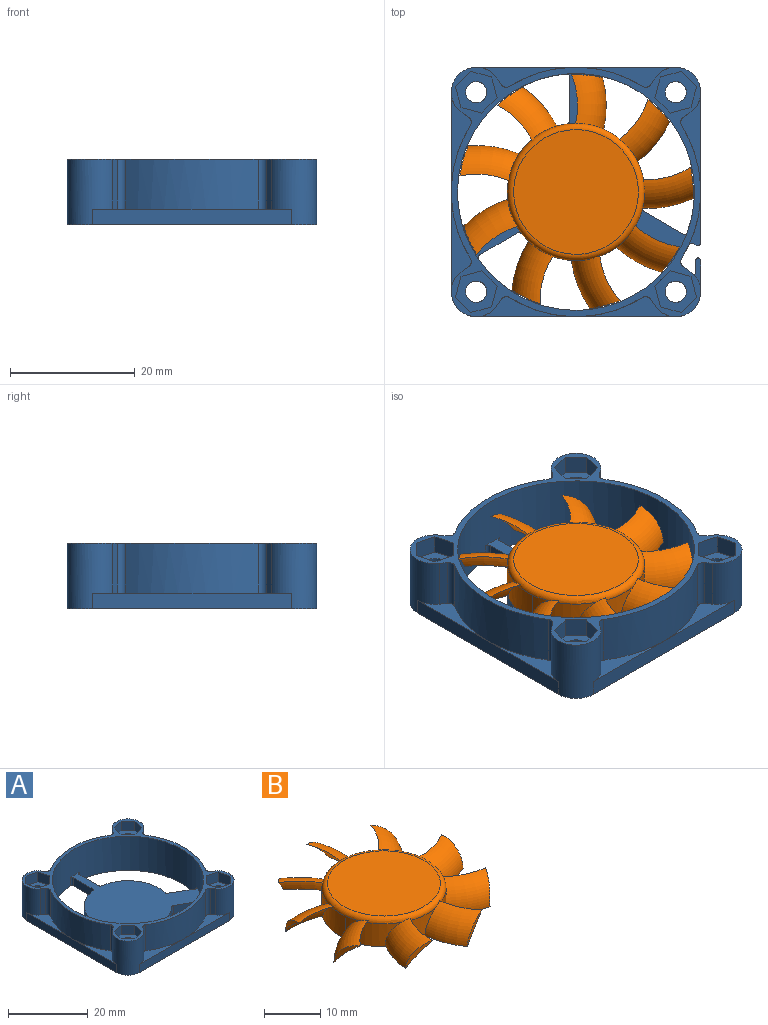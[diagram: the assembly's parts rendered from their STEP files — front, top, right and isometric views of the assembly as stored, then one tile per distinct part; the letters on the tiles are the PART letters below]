
ASSEMBLY  parts=2 mates=1
PART A: 115 faces, bbox 40x40x10.5 mm
  f0: plane 10.28x5.94mm, normal (0.5,0.87,0), area 17.8mm2, adj f19,f33,f35,f80,f81,f82
  f1: plane 2.5x1.78mm, normal (-1,0,0), area 4.5mm2, adj f8,f33,f81,f97
  f2: plane 16x3.21mm, normal (0,0,1), area 18mm2, adj f26,f27,f56,f57,f100
  f3: plane 16x3.21mm, normal (0,0,1), area 18mm2, adj f25,f26,f65,f69,f106
  f4: plane 16x3.21mm, normal (0,0,1), area 18mm2, adj f21,f22,f34,f60,f102
  f5: plane 16x3.21mm, normal (0,0,1), area 18mm2, adj f23,f24,f62,f63,f104
  f6: plane 16x3.21mm, normal (0,0,1), area 18mm2, adj f27,f28,f57,f58,f101
  f7: plane 35.04x31.24mm, normal (0,0,1), area 457.1mm2, adj f12,f13,f14,f15,f16,f17,f18,f30
  f8: plane 5.45x1.07mm, normal (0,0,1), area 3mm2, adj f1,f28,f29,f81,f96,f97
  f9: plane 16x3.21mm, normal (0,0,1), area 18mm2, adj f22,f23,f61,f62,f103
  f10: plane 8.58x1.89mm, normal (0,0,1), area 5.1mm2, adj f20,f21,f34,f76,f89
  f11: plane 16x3.21mm, normal (0,0,1), area 18mm2, adj f24,f25,f64,f65,f105
  f12: plane 7.04x2.5mm, normal (1,0,0), area 17.6mm2, adj f7,f33,f87,f92
  f13: cylinder r=19mm len=38mm, axis (0,0,1), area 1221.3mm2, adj f7,f33,f71,f83,f84,f85,f86,f87
  f14: plane 6.22x3.59mm, normal (0.5,0.87,0), area 18mm2, adj f7,f33,f88,f95
  f15: plane 6.09x3.52mm, normal (0.5,-0.87,0), area 17.6mm2, adj f7,f33,f84,f90
  f16: cylinder r=11mm len=16.31mm, axis (0,0,1), area 46.1mm2, adj f7,f33,f90,f94
  f17: plane 6.09x3.52mm, normal (-0.5,0.87,0), area 17.6mm2, adj f7,f33,f85,f91
  f18: plane 7.04x2.5mm, normal (-1,0,0), area 17.6mm2, adj f7,f33,f86,f93
  f19: cylinder r=11mm len=3.9mm, axis (0,0,1), area 6.7mm2, adj f0,f20,f33,f35,f77
  f20: plane 8.8x5.08mm, normal (-0.5,-0.87,0), area 11.1mm2, adj f10,f19,f33,f76,f77,f78,f89
  f21: plane 24.08x2.5mm, normal (1,0,0), area 60.2mm2, adj f4,f10,f22,f33,f89
  f22: cylinder r=4mm len=10.5mm, axis (0,0,1), area 127.6mm2, adj f4,f9,f21,f23,f33,f60,f61,f71
  f23: plane 32x2.5mm, normal (0,1,0), area 80mm2, adj f5,f9,f22,f24,f33
  f24: cylinder r=4mm len=10.5mm, axis (0,0,1), area 127.6mm2, adj f5,f11,f23,f25,f33,f63,f64,f71
  f25: plane 32x2.5mm, normal (-1,0,0), area 80mm2, adj f3,f11,f24,f26,f33
  f26: cylinder r=4mm len=10.5mm, axis (0,0,1), area 127.6mm2, adj f2,f3,f25,f27,f33,f56,f69,f71
  f27: plane 32x2.5mm, normal (0,-1,0), area 80mm2, adj f2,f6,f26,f28,f33
  f28: cylinder r=4mm len=10.5mm, axis (0,0,1), area 128mm2, adj f6,f8,f27,f29,f33,f58,f59,f71
  f29: plane 4.96x2.5mm, normal (1,0,0), area 12.4mm2, adj f8,f28,f33,f96
  f30: plane 6.22x3.59mm, normal (-0.5,-0.87,0), area 18mm2, adj f7,f33,f83,f94
  f31: cylinder r=11mm len=15.12mm, axis (0,0,1), area 50.4mm2, adj f7,f33,f91,f93
  f32: cylinder r=11mm len=13.49mm, axis (0,0,1), area 46.1mm2, adj f7,f33,f92,f95
  f33: plane 40x40mm, normal (0,0,-1), area 793.4mm2, adj f0,f1,f12,f13,f14,f15,f16,f17
  f34: cylinder r=20mm len=21.25mm, axis (0,0,1), area 180.4mm2, adj f4,f10,f71,f76,f79,f98,f102
  f35: plane 9.49x8.4mm, normal (0,0,-1), area 34.2mm2, adj f0,f19,f77,f79,f80
  f36: plane 3.35x3mm, normal (-0.26,-0.97,0), area 10.4mm2, adj f37,f70,f71,f75
  f37: plane 3.35x3mm, normal (-0.97,-0.26,0), area 10.4mm2, adj f36,f38,f71,f75
  f38: plane 3x2.45mm, normal (-0.71,0.71,0), area 10.4mm2, adj f37,f39,f71,f75
  f39: plane 3.35x3mm, normal (0.26,0.97,0), area 10.4mm2, adj f38,f40,f71,f75
  f40: plane 3.35x3mm, normal (0.97,0.26,0), area 10.4mm2, adj f39,f70,f71,f75
  f41: plane 3x2.45mm, normal (-0.71,0.71,0), area 10.4mm2, adj f42,f66,f71,f73
  f42: plane 3.35x3mm, normal (0.26,0.97,0), area 10.4mm2, adj f41,f43,f71,f73
  f43: plane 3.35x3mm, normal (0.97,0.26,0), area 10.4mm2, adj f42,f44,f71,f73
  f44: plane 3x2.45mm, normal (0.71,-0.71,0), area 10.4mm2, adj f43,f45,f71,f73
  f45: plane 3.35x3mm, normal (-0.26,-0.97,0), area 10.4mm2, adj f44,f66,f71,f73
  f46: plane 3.35x3mm, normal (-0.97,0.26,0), area 10.4mm2, adj f47,f67,f71,f72
  f47: plane 3.35x3mm, normal (-0.26,0.97,0), area 10.4mm2, adj f46,f48,f71,f72
  f48: plane 3x2.45mm, normal (0.71,0.71,0), area 10.4mm2, adj f47,f49,f71,f72
  f49: plane 3.35x3mm, normal (0.97,-0.26,0), area 10.4mm2, adj f48,f50,f71,f72
  f50: plane 3.35x3mm, normal (0.26,-0.97,0), area 10.4mm2, adj f49,f67,f71,f72
  f51: plane 3x2.45mm, normal (-0.71,-0.71,0), area 10.4mm2, adj f52,f68,f71,f74
  f52: plane 3.35x3mm, normal (-0.97,0.26,0), area 10.4mm2, adj f51,f53,f71,f74
  f53: plane 3.35x3mm, normal (-0.26,0.97,0), area 10.4mm2, adj f52,f54,f71,f74
  f54: plane 3x2.45mm, normal (0.71,0.71,0), area 10.4mm2, adj f53,f55,f71,f74
  f55: plane 3.35x3mm, normal (0.97,-0.26,0), area 10.4mm2, adj f54,f68,f71,f74
  f56: plane 8x1.06mm, normal (0.82,-0.57,0), area 10.4mm2, adj f2,f26,f71,f100
  f57: cylinder r=20mm len=21.25mm, axis (0,0,-1), area 179.2mm2, adj f2,f6,f71,f100,f101
  f58: plane 8x1.06mm, normal (-0.82,-0.57,0), area 10.4mm2, adj f6,f28,f71,f101
  f59: plane 8.5x1.06mm, normal (0.57,0.82,0), area 11mm2, adj f28,f71,f80,f98
  f60: plane 8x1.06mm, normal (0.57,-0.82,0), area 10.4mm2, adj f4,f22,f71,f102
  f61: plane 8x1.06mm, normal (-0.82,0.57,0), area 10.4mm2, adj f9,f22,f71,f103
  f62: cylinder r=20mm len=21.25mm, axis (0,0,-1), area 179.2mm2, adj f5,f9,f71,f103,f104
  f63: plane 8x1.06mm, normal (0.82,0.57,0), area 10.4mm2, adj f5,f24,f71,f104
  f64: plane 8x1.06mm, normal (-0.57,-0.82,0), area 10.4mm2, adj f11,f24,f71,f105
  f65: cylinder r=20mm len=21.25mm, axis (0,0,-1), area 179.2mm2, adj f3,f11,f71,f105,f106
  f66: plane 3.35x3mm, normal (-0.97,-0.26,0), area 10.4mm2, adj f41,f45,f71,f73
  f67: plane 3x2.45mm, normal (-0.71,-0.71,0), area 10.4mm2, adj f46,f50,f71,f72
  f68: plane 3.35x3mm, normal (0.26,-0.97,0), area 10.4mm2, adj f51,f55,f71,f74
  f69: plane 8x1.06mm, normal (-0.57,0.82,0), area 10.4mm2, adj f3,f26,f71,f106
  f70: plane 3x2.45mm, normal (0.71,-0.71,0), area 10.4mm2, adj f36,f40,f71,f75
  f71: plane 40x40mm, normal (0,0,1), area 183.3mm2, adj f13,f22,f24,f26,f28,f34,f36,f37
  f72: plane 6.69x6.69mm, normal (0,0,1), area 22.1mm2, adj f46,f47,f48,f49,f50,f67,f111
  f73: plane 6.69x6.69mm, normal (0,0,1), area 22.1mm2, adj f41,f42,f43,f44,f45,f66,f109
  f74: plane 6.69x6.69mm, normal (0,0,1), area 22.1mm2, adj f51,f52,f53,f54,f55,f68,f107
  f75: plane 6.69x6.69mm, normal (0,0,1), area 22.1mm2, adj f36,f37,f38,f39,f40,f70,f113
  f76: cylinder r=0.5mm len=0.7mm, axis (0,0,1), area 0.4mm2, adj f10,f20,f34,f78
  f77: cylinder r=0.5mm len=7.74mm, axis (0.87,-0.5,0), area 6.8mm2, adj f19,f20,f35,f78
  f78: bspline ~1.22x1.19mm, area 0.9mm2, adj f20,f76,f77,f79
  f79: torus R=19.5mm, axis (0,0,1), area 2.5mm2, adj f34,f35,f78,f99
  f80: cylinder r=0.5mm len=2.57mm, axis (0.82,-0.57,0), area 1.5mm2, adj f0,f35,f59,f82,f99
  f81: cylinder r=0.5mm len=2.5mm, axis (0,0,-1), area 2.3mm2, adj f0,f1,f8,f28,f33,f82
  f82: torus R=3.5mm, axis (0,0,1), area 0.4mm2, adj f0,f28,f80,f81
  f83: cylinder r=0.5mm len=2.5mm, axis (0,0,1), area 2.2mm2, adj f7,f13,f30,f33
  f84: cylinder r=0.5mm len=2.5mm, axis (0,0,1), area 2.1mm2, adj f7,f13,f15,f33
  f85: cylinder r=0.5mm len=2.5mm, axis (0,0,1), area 2.1mm2, adj f7,f13,f17,f33
  f86: cylinder r=0.5mm len=2.5mm, axis (0,0,1), area 2.1mm2, adj f7,f13,f18,f33
  f87: cylinder r=0.5mm len=2.5mm, axis (0,0,1), area 2.1mm2, adj f7,f12,f13,f33
  f88: cylinder r=0.5mm len=2.5mm, axis (0,0,1), area 2.2mm2, adj f7,f13,f14,f33
  f89: cylinder r=0.5mm len=2.5mm, axis (0,0,-1), area 2.6mm2, adj f10,f20,f21,f33
  f90: cylinder r=0.5mm len=2.5mm, axis (0,0,1), area 1.8mm2, adj f7,f15,f16,f33
  f91: cylinder r=0.5mm len=2.5mm, axis (0,0,1), area 1.8mm2, adj f7,f17,f31,f33
  f92: cylinder r=0.5mm len=2.5mm, axis (0,0,1), area 1.8mm2, adj f7,f12,f32,f33
  f93: cylinder r=0.5mm len=2.5mm, axis (0,0,1), area 1.8mm2, adj f7,f18,f31,f33
  f94: cylinder r=0.5mm len=2.5mm, axis (0,0,1), area 1.6mm2, adj f7,f16,f30,f33
  f95: cylinder r=0.5mm len=2.5mm, axis (0,0,1), area 1.6mm2, adj f7,f14,f32,f33
  f96: cylinder r=0.5mm len=2.5mm, axis (0,0,1), area 1.7mm2, adj f8,f29,f33,f97
  f97: cylinder r=0.5mm len=2.5mm, axis (0,0,1), area 1.7mm2, adj f1,f8,f33,f96
  f98: cylinder r=1mm len=8.5mm, axis (0,0,1), area 12.9mm2, adj f34,f59,f71,f99
  f99: bspline ~1.5x1.35mm, area 0.5mm2, adj f79,f80,f98
  f100: cylinder r=1mm len=8mm, axis (0,0,-1), area 12.2mm2, adj f2,f56,f57,f71
  f101: cylinder r=1mm len=8mm, axis (0,0,-1), area 12.2mm2, adj f6,f57,f58,f71
  f102: cylinder r=1mm len=8mm, axis (0,0,1), area 12.2mm2, adj f4,f34,f60,f71
  f103: cylinder r=1mm len=8mm, axis (0,0,-1), area 12.2mm2, adj f9,f61,f62,f71
  f104: cylinder r=1mm len=8mm, axis (0,0,-1), area 12.2mm2, adj f5,f62,f63,f71
  f105: cylinder r=1mm len=8mm, axis (0,0,-1), area 12.2mm2, adj f11,f64,f65,f71
  f106: cylinder r=1mm len=8mm, axis (0,0,-1), area 12.2mm2, adj f3,f65,f69,f71
  f107: cylinder r=1.7mm len=6.95mm, axis (0,0,-1), area 74.2mm2, adj f74,f108
  f108: cone r=1.7mm half-angle=45deg, axis (0,0,-1), area 9.7mm2, adj f33,f107
  f109: cylinder r=1.7mm len=6.95mm, axis (0,0,-1), area 74.2mm2, adj f73,f110
  f110: cone r=1.7mm half-angle=45deg, axis (0,0,-1), area 9.7mm2, adj f33,f109
  f111: cylinder r=1.7mm len=6.95mm, axis (0,0,-1), area 74.2mm2, adj f72,f112
  f112: cone r=1.7mm half-angle=45deg, axis (0,0,-1), area 9.7mm2, adj f33,f111
  f113: cylinder r=1.7mm len=6.95mm, axis (0,0,-1), area 74.2mm2, adj f75,f114
  f114: cone r=1.7mm half-angle=45deg, axis (0,0,-1), area 9.7mm2, adj f33,f113
PART B: 32 faces, bbox 42.3x42.5x6 mm
  f0: cylinder r=11mm len=22mm, axis (0,0,-1), area 307.6mm2, adj f1,f3,f4,f5,f6,f8,f9,f11
  f1: cylinder r=11mm len=4.52mm, axis (0,0,-1), area 3.9mm2, adj f0,f4,f11
  f2: plane 20x20mm, normal (0,0,1), area 314.2mm2, adj f4
  f3: plane 22x22mm, normal (0,0,-1), area 380.1mm2, adj f0
  f4: torus R=10mm, axis (0,0,1), area 102.2mm2, adj f0,f1,f2,f5,f6,f8,f9,f11
  f5: torus R=12.73mm, axis (0,0,-1), area 60.3mm2, adj f0,f4,f6,f7
  f6: torus R=5.4mm, axis (0,0,-1), area 55.4mm2, adj f0,f4,f5,f7
  f7: cylinder r=18.8mm len=4.97mm, axis (0,0,1), area 4.5mm2, adj f5,f6
  f8: torus R=12.73mm, axis (0,0,-1), area 60.3mm2, adj f0,f4,f9,f10
  f9: torus R=5.4mm, axis (0,0,-1), area 55.4mm2, adj f0,f4,f8,f10
  f10: cylinder r=18.8mm len=4.97mm, axis (0,0,1), area 4.5mm2, adj f8,f9
  f11: torus R=12.73mm, axis (0,0,-1), area 60.3mm2, adj f0,f1,f4,f12,f13
  f12: torus R=5.4mm, axis (0,0,-1), area 55.4mm2, adj f0,f4,f11,f13
  f13: cylinder r=18.8mm len=4.97mm, axis (0,0,1), area 4.5mm2, adj f11,f12
  f14: torus R=12.73mm, axis (0,0,-1), area 60.3mm2, adj f0,f4,f15,f16
  f15: torus R=5.4mm, axis (0,0,-1), area 55.4mm2, adj f0,f4,f14,f16
  f16: cylinder r=18.8mm len=4.97mm, axis (0,0,1), area 4.5mm2, adj f14,f15
  f17: torus R=12.73mm, axis (0,0,-1), area 60.3mm2, adj f0,f4,f18,f19
  f18: torus R=5.4mm, axis (0,0,-1), area 55.4mm2, adj f0,f4,f17,f19
  f19: cylinder r=18.8mm len=4.97mm, axis (0,0,1), area 4.5mm2, adj f17,f18
  f20: torus R=12.73mm, axis (0,0,-1), area 60.3mm2, adj f0,f4,f21,f22
  f21: torus R=5.4mm, axis (0,0,-1), area 55.4mm2, adj f0,f4,f20,f22
  f22: cylinder r=18.8mm len=4.99mm, axis (0,0,1), area 4.5mm2, adj f20,f21
  f23: torus R=12.73mm, axis (0,0,-1), area 60.3mm2, adj f0,f4,f24,f25
  f24: torus R=5.4mm, axis (0,0,-1), area 55.4mm2, adj f0,f4,f23,f25
  f25: cylinder r=18.8mm len=4.97mm, axis (0,0,1), area 4.5mm2, adj f23,f24
  f26: torus R=12.73mm, axis (0,0,-1), area 60.3mm2, adj f0,f4,f27,f28
  f27: torus R=5.4mm, axis (0,0,-1), area 55.4mm2, adj f0,f4,f26,f28
  f28: cylinder r=18.8mm len=5mm, axis (0,0,1), area 4.5mm2, adj f26,f27
  f29: torus R=12.73mm, axis (0,0,-1), area 60.3mm2, adj f0,f4,f30,f31
  f30: torus R=5.4mm, axis (0,0,-1), area 55.4mm2, adj f0,f4,f29,f31
  f31: cylinder r=18.8mm len=4.97mm, axis (0,0,1), area 4.5mm2, adj f29,f30
PLACE A at identity
PLACE B t=(0,0,-1)mm
MATE fastened B.f0 <-> A.f13  axis (0,0,-1) through (0,0,0)mm
